# Revit family: Accessory-Teknion-EMWS_Wall-Shelf_with_Thought_Board-R2016
name_source: partatom
category: Furniture
revit_build: Autodesk Revit 2018 (Build: 20190510_1515(x64)
units: mm (PartAtom-declared; Revit-internal decimal feet)

## family parameters
Always vertical = Yes
Cut with Voids When Loaded = No
OmniClass Number = 23.40.20.00
OmniClass Title = General Furniture and Specialties
Room Calculation Point = No
Shared = Yes
Work Plane-Based = No

## types (5) — shared parameters
Assembly Code = E2020200
Description = Emote Wall Shelf with Thought Board
Manufacturer = Teknion
Manufacturer Fax = 416.661.4586
Model = EMWS__
Part Number = EMWS
Product Documentation Link = https://assets.teknion.com
Product Line = Emote
Product Page URL = https://www.teknion.com
Series = Emote
Sustainability Data = https://www.teknion.com
URL = www.teknion.com
Unit Weight URL = http://www.teknion.com
Warranty = http://www.teknion.com

## per-type parameters (varying)
| type | Wall Shelf with Glass Thought Board |
| Wall Shelf with Flintwood Thought Board | No |
| Wall Shelf with Chroma Wood Thought Board | No |
| Wall Shelf with Veneer Thought Board | No |
| Wall Shelf with Backpainted Glass Thought Board | Yes |
| Wall Shelf with Fabric Thought Board | No |

type visibility flags (boolean, named after types; folded from table):
- Wall Shelf with Flintwood Thought Board: Yes: Wall Shelf with Flintwood Thought Board
- Wall Shelf with Chroma Wood Thought Board: Yes: Wall Shelf with Chroma Wood Thought Board
- Wall Shelf with Veneer Thought Board: Yes: Wall Shelf with Veneer Thought Board
- Wall Shelf with Backpainted Glass Thought Board: Yes: (none)
- Wall Shelf with Fabric Thought Board: Yes: Wall Shelf with Fabric Thought Board

## geometry (parser evidence)
native form markers: Blend x31, Sweep x2
no freeform markers — native parametric forms only
